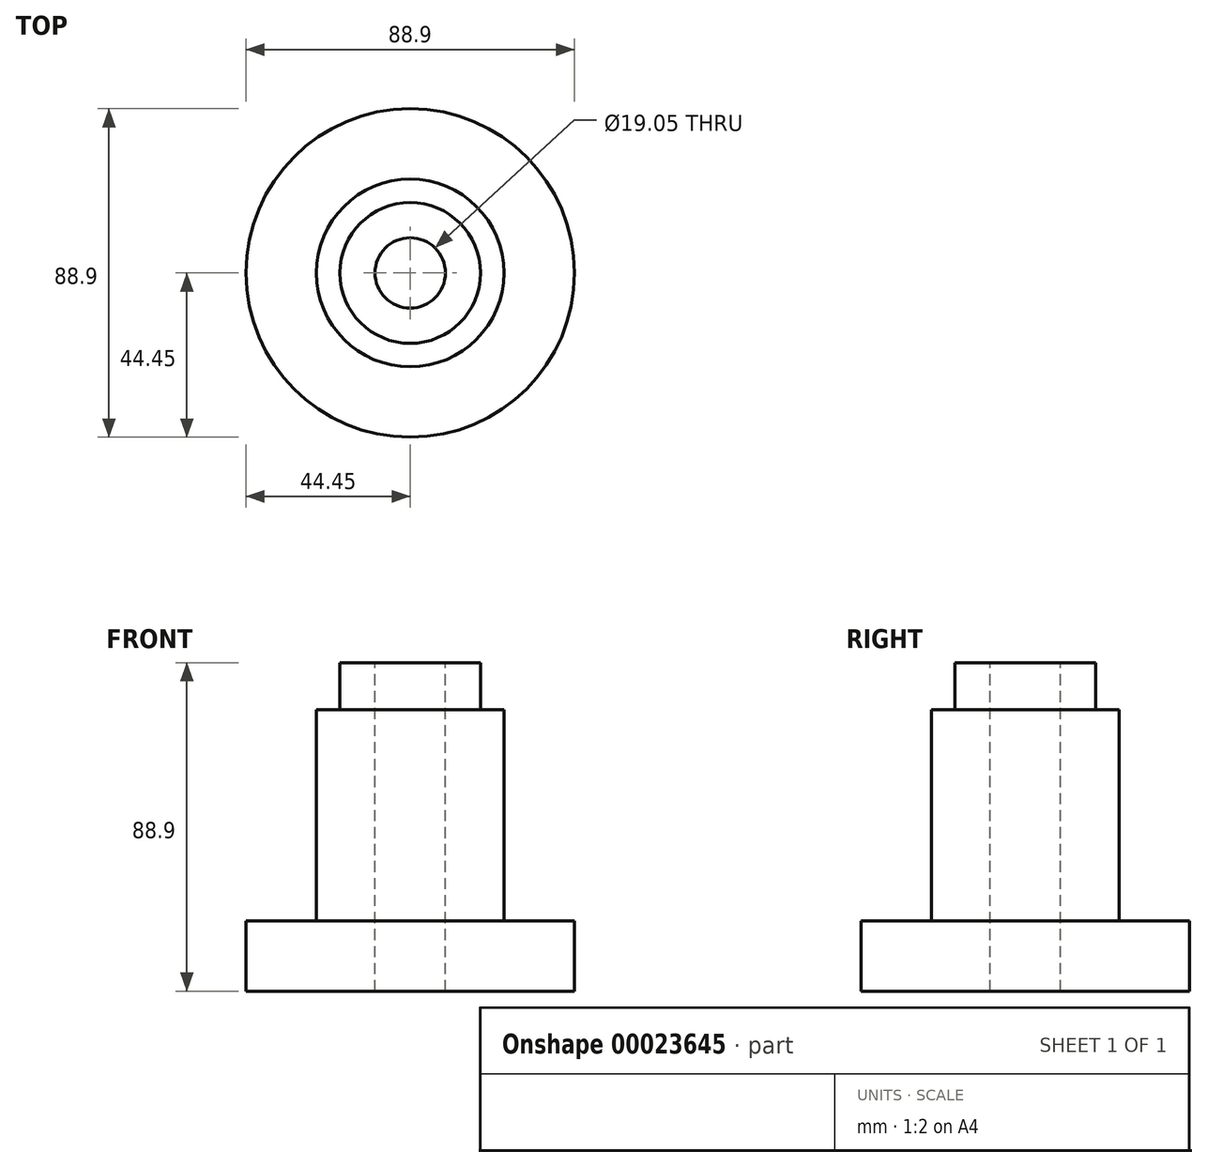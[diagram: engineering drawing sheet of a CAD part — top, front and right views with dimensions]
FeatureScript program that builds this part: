
annotation { "Feature Type Name" : "Feature", "Feature Type Description" : "" }
export const myFeature = defineFeature(function(context is Context, id is Id, definition is map)
    precondition{}
    {
        {
            var Q0;
            Q0=qCreatedBy(makeId("Front.planeOp"),FACE);
            var sketch = newSketch(context, id + "F0", { "sketchPlane" : qUnion([Q0])});
            skLineSegment(sketch, "E0", {"start": v(0, 0) * mm, "end": v(0, 75.08) * mm, "construction": true});
            skLineSegment(sketch, "E1", {"start": v(0, 75.08) * mm, "end": v(0, -67.9) * mm, "construction": true});
            skLineSegment(sketch, "E2", {"start": v(0, -67.9) * mm, "end": v(0, 0) * mm, "construction": true});
            skLineSegment(sketch, "E3.bottom", {"start": v(-9.52, -56.37) * mm, "end": v(-44.45, -56.37) * mm});
            skLineSegment(sketch, "E3.top", {"start": v(-9.52, -37.32) * mm, "end": v(-44.45, -37.32) * mm});
            skLineSegment(sketch, "E3.left", {"start": v(-9.52, -56.37) * mm, "end": v(-9.52, -37.32) * mm});
            skLineSegment(sketch, "E3.right", {"start": v(-44.45, -56.37) * mm, "end": v(-44.45, -37.32) * mm});
            skLineSegment(sketch, "E4.bottom", {"start": v(-9.52, -37.32) * mm, "end": v(-25.4, -37.32) * mm});
            skLineSegment(sketch, "E4.top", {"start": v(-9.53, 19.83) * mm, "end": v(-25.4, 19.83) * mm});
            skLineSegment(sketch, "E4.left", {"start": v(-9.52, -37.32) * mm, "end": v(-9.53, 19.83) * mm});
            skLineSegment(sketch, "E4.right", {"start": v(-25.4, -37.32) * mm, "end": v(-25.4, 19.83) * mm});
            skLineSegment(sketch, "E5.bottom", {"start": v(-9.53, 19.83) * mm, "end": v(-19.05, 19.83) * mm});
            skLineSegment(sketch, "E5.top", {"start": v(-9.53, 32.53) * mm, "end": v(-19.05, 32.53) * mm});
            skLineSegment(sketch, "E5.left", {"start": v(-9.53, 19.83) * mm, "end": v(-9.53, 32.53) * mm});
            skLineSegment(sketch, "E5.right", {"start": v(-19.05, 19.83) * mm, "end": v(-19.05, 32.53) * mm});
            skSolve(sketch);
        }
        {
            var Q0;
            Q0 = qSketchRegion(id + "F0", true);
            var Q1;
            Q1=sQuery(id+"F0.wireOp",EDGE,"E1");
            revolve(context, id + "F1", {"entities" : qUnion([Q0]), "axis" : qUnion([Q1]), "revolveType" : RevolveType.FULL});
        }
    });
